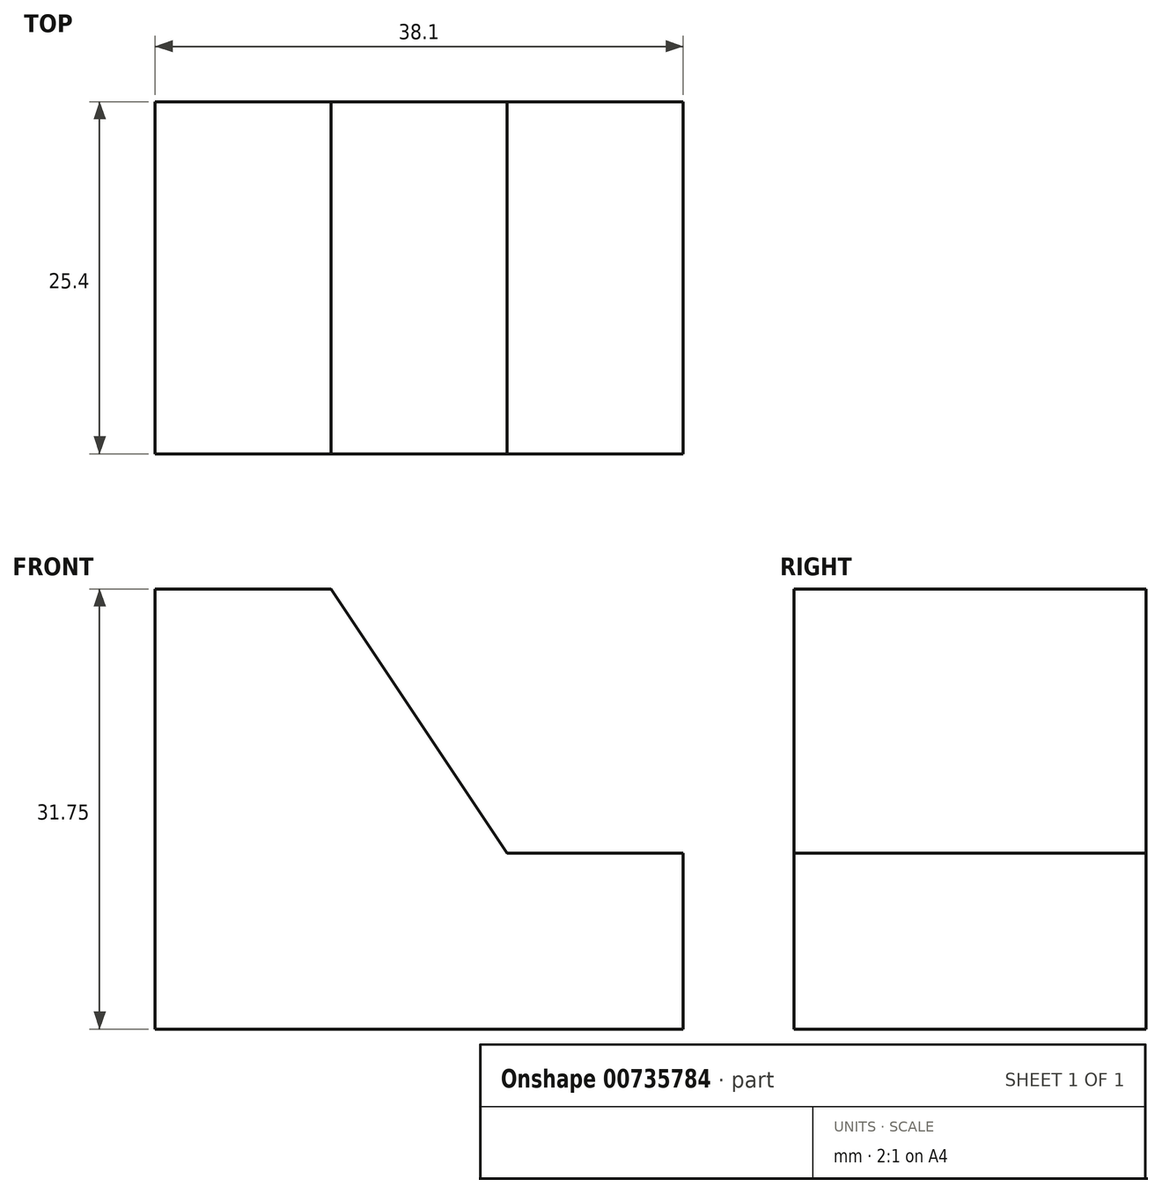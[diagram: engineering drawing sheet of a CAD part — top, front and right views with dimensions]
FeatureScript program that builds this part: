
annotation { "Feature Type Name" : "Feature", "Feature Type Description" : "" }
export const myFeature = defineFeature(function(context is Context, id is Id, definition is map)
    precondition{}
    {
        {
            var Q0;
            Q0=qCreatedBy(makeId("Front.planeOp"),FACE);
            var sketch = newSketch(context, id + "F0", { "sketchPlane" : qUnion([Q0])});
            skLineSegment(sketch, "E0", {"start": v(0, 0) * mm, "end": v(38.1, 0) * mm});
            skLineSegment(sketch, "E1", {"start": v(38.1, 0) * mm, "end": v(38.1, 12.7) * mm});
            skLineSegment(sketch, "E2", {"start": v(38.1, 12.7) * mm, "end": v(25.4, 12.7) * mm});
            skLineSegment(sketch, "E3", {"start": v(25.4, 12.7) * mm, "end": v(25.4, 31.75) * mm});
            skLineSegment(sketch, "E4", {"start": v(25.4, 31.75) * mm, "end": v(0, 31.75) * mm});
            skLineSegment(sketch, "E5", {"start": v(0, 31.75) * mm, "end": v(0, 0) * mm});
            skSolve(sketch);
        }
        {
            var Q0;
            Q0=makeQuery(id+"F0.imprint","IMPRINT",FACE,{"disambiguationData":[TD([[makeQuery(id+"F0.imprint","IMPRINT",EDGE,{"derivedFrom":sQuery(id+"F0.wireOp",EDGE,"E0")}),1.0]])]});
            extrude(context, id + "F1", {"entities" : qUnion([Q0]), "depth" : 25.4 * mm, "offsetDistance" : 25.4 * mm});
        }
        {
            var Q0;
            Q0=makeQuery(id+"F1.opExtrude","CAP_FACE",FACE,{"disambiguationData":[OSD([sQuery(id+"F0.wireOp",EDGE,"E0"),sQuery(id+"F0.wireOp",EDGE,"E1"),sQuery(id+"F0.wireOp",EDGE,"E2"),sQuery(id+"F0.wireOp",EDGE,"E3"),sQuery(id+"F0.wireOp",EDGE,"E4"),sQuery(id+"F0.wireOp",EDGE,"E5")])],"isStart":false});
            var sketch = newSketch(context, id + "F2", { "sketchPlane" : qUnion([Q0])});
            skLineSegment(sketch, "E6", {"start": v(12.7, 31.75) * mm, "end": v(25.4, 12.7) * mm});
            skSolve(sketch);
        }
        {
            var Q0;
            Q0 = qSketchRegion(id + "F2", true);
            var Q1;
            {var subQ0=sQuery(id+"F2.wireOp",EDGE,"E6");Q1=makeQuery(id+"F2.imprint","IMPRINT",FACE,{"disambiguationData":[TD([[makeQuery(id+"F2.imprint","IMPRINT",EDGE,{"derivedFrom":subQ0}),1.0]])]});}
            extrude(context, id + "F3", {"entities" : qUnion([Q0, Q1]), "operationType" : NewBodyOperationType.REMOVE, "oppositeDirection" : true, "depth" : 25.4 * mm, "offsetDistance" : 25.4 * mm});
        }
    });
